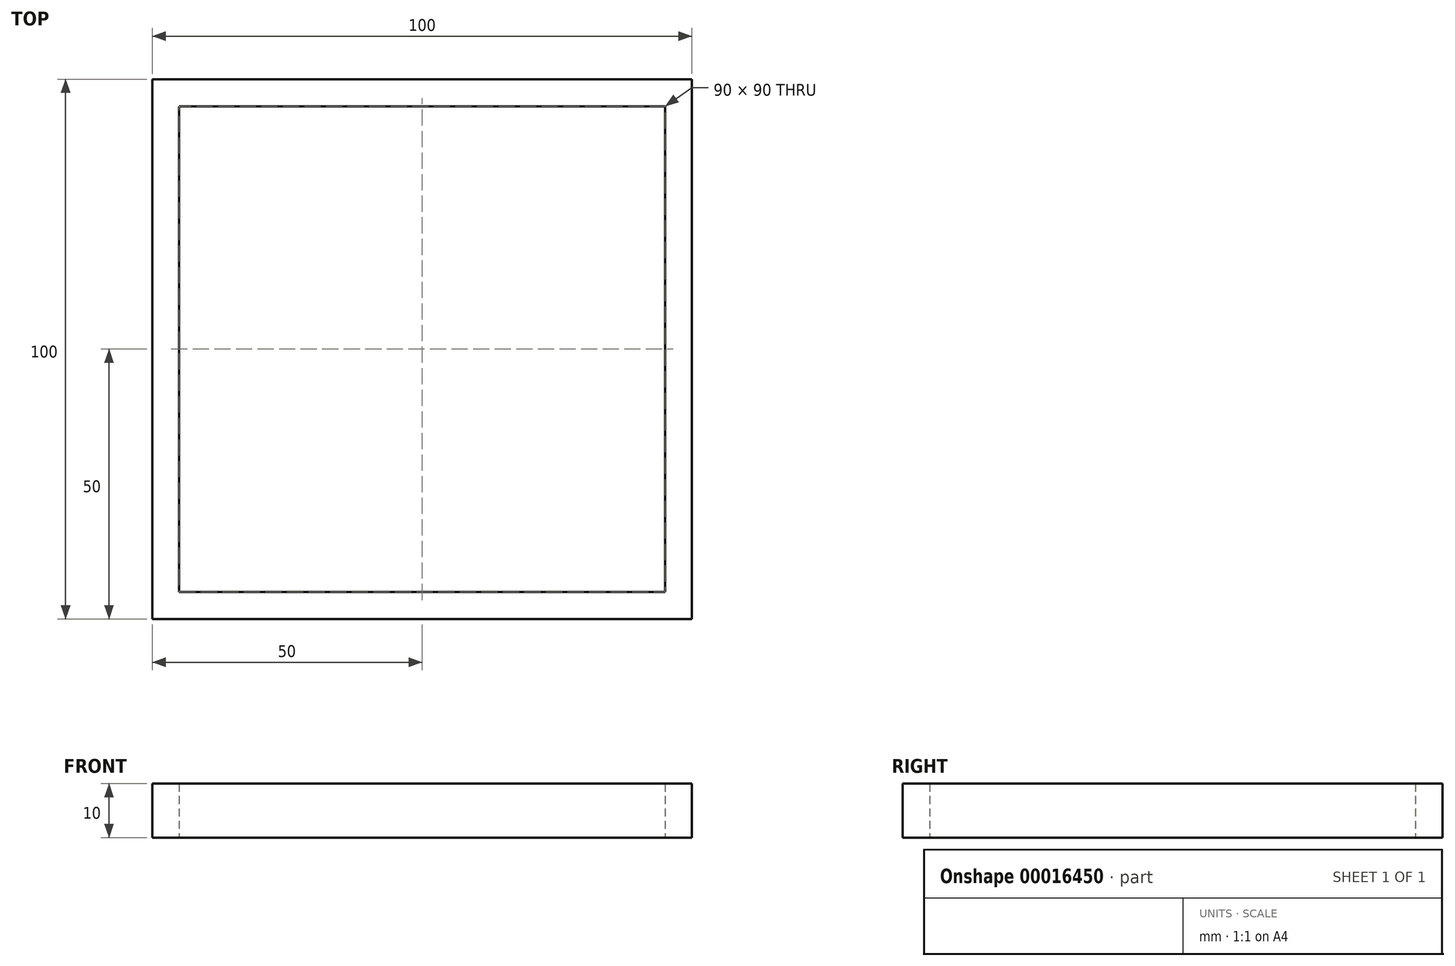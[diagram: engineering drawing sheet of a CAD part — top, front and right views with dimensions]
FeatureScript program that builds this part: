
annotation { "Feature Type Name" : "Feature", "Feature Type Description" : "" }
export const myFeature = defineFeature(function(context is Context, id is Id, definition is map)
    precondition{}
    {
        {
            var Q0;
            Q0=qCreatedBy(makeId("Top.planeOp"),FACE);
            var sketch = newSketch(context, id + "F0", { "sketchPlane" : qUnion([Q0])});
            skLineSegment(sketch, "E0.bottom", {"start": v(50, -50) * mm, "end": v(-50, -50) * mm});
            skLineSegment(sketch, "E0.top", {"start": v(50, 50) * mm, "end": v(-50, 50) * mm});
            skLineSegment(sketch, "E0.left", {"start": v(50, -50) * mm, "end": v(50, 50) * mm});
            skLineSegment(sketch, "E0.right", {"start": v(-50, -50) * mm, "end": v(-50, 50) * mm});
            skPoint(sketch, "E0.middle", {"position": v(0, 0) * mm});
            skLineSegment(sketch, "E1.bottom", {"start": v(45, -45) * mm, "end": v(-45, -45) * mm});
            skLineSegment(sketch, "E1.top", {"start": v(45, 45) * mm, "end": v(-45, 45) * mm});
            skLineSegment(sketch, "E1.left", {"start": v(45, -45) * mm, "end": v(45, 45) * mm});
            skLineSegment(sketch, "E1.right", {"start": v(-45, -45) * mm, "end": v(-45, 45) * mm});
            skSolve(sketch);
        }
        {
            var Q0;
            Q0=makeQuery(id+"F0.imprint","IMPRINT",FACE,{"disambiguationData":[TD([[makeQuery(id+"F0.imprint","IMPRINT",EDGE,{"derivedFrom":sQuery(id+"F0.wireOp",EDGE,"E0.bottom")}),-1.0]])]});
            extrude(context, id + "F1", {"entities" : qUnion([Q0]), "depth" : 10 * mm});
        }
    });
